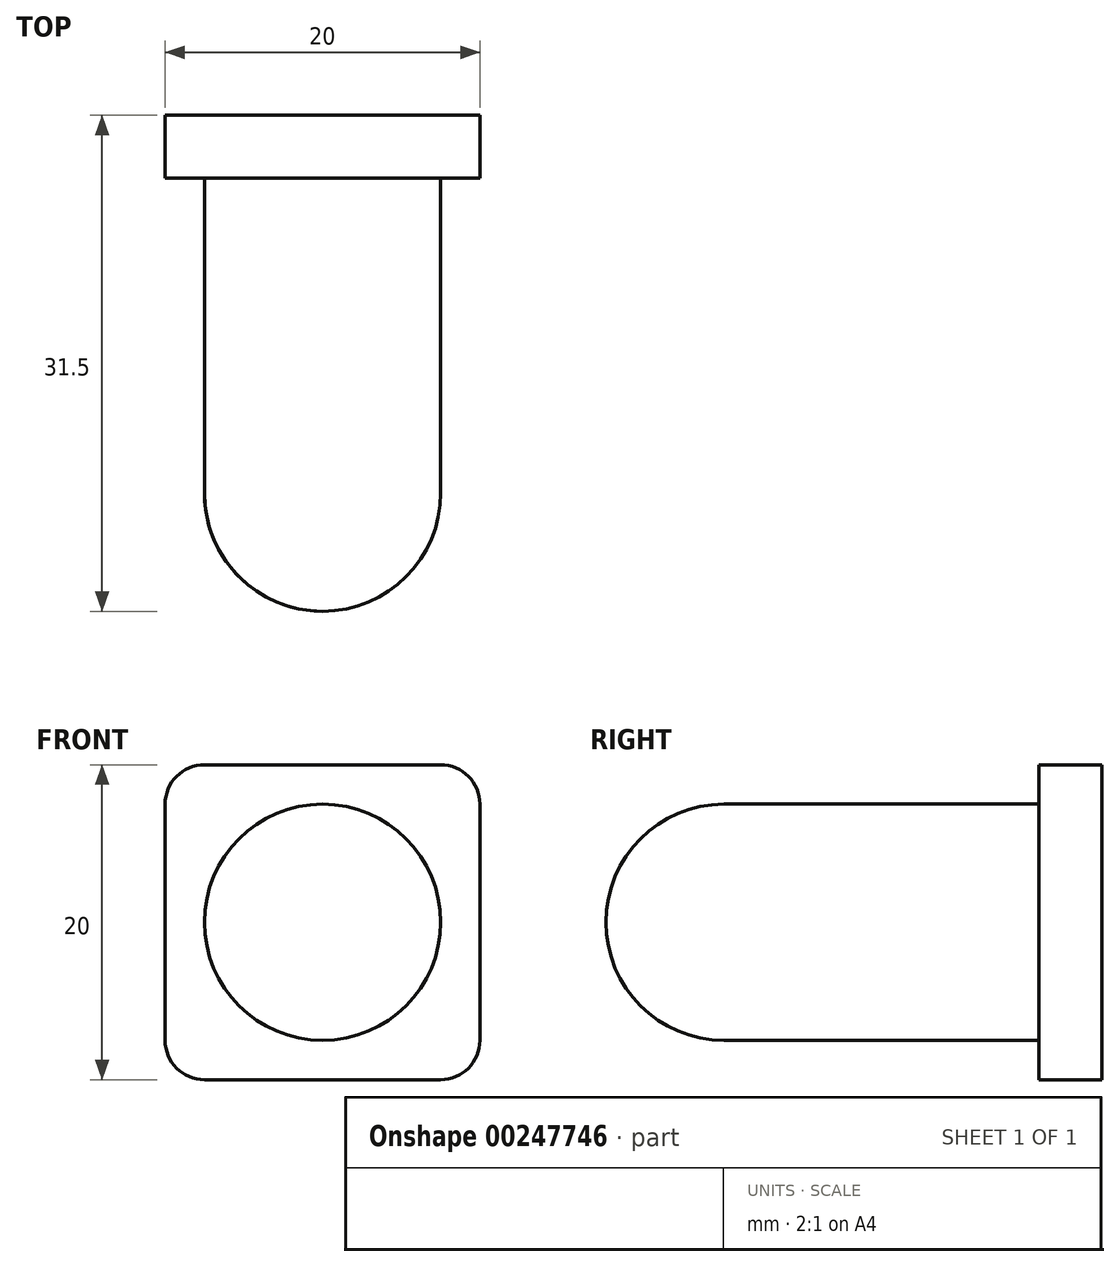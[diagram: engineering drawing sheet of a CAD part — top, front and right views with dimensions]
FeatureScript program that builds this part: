
annotation { "Feature Type Name" : "Feature", "Feature Type Description" : "" }
export const myFeature = defineFeature(function(context is Context, id is Id, definition is map)
    precondition{}
    {
        {
            var Q0;
            Q0=qCreatedBy(makeId("Top.planeOp"),FACE);
            var sketch = newSketch(context, id + "F0", { "sketchPlane" : qUnion([Q0])});
            skCircle(sketch, "E0", {"center": v(0, 0) * mm, "radius": 7.5 * mm});
            skLineSegment(sketch, "E1", {"start": v(-7.5, 0) * mm, "end": v(7.5, 0) * mm});
            skLineSegment(sketch, "E2", {"start": v(0, 0) * mm, "end": v(0, -7.5) * mm});
            skSolve(sketch);
        }
        {
            var Q0;
            {var subQ3=sQuery(id+"F0.wireOp",EDGE,"E2");Q0=makeQuery(id+"F0.imprint","IMPRINT",FACE,{"disambiguationData":[TD([[makeQuery(id+"F0.imprint","IMPRINT",EDGE,{"derivedFrom":subQ3}),1.0]])]});}
            var Q1;
            Q1=sQuery(id+"F0.wireOp",EDGE,"E2");
            revolve(context, id + "F1", {"entities" : qUnion([Q0]), "axis" : qUnion([Q1]), "revolveType" : RevolveType.FULL});
        }
        {
            var Q0;
            Q0=makeQuery(id+"F1.opRevolve","SWEPT_FACE",FACE,{"disambiguationData":[OSD([sQuery(id+"F0.wireOp",EDGE,"E1")])]});
            var sketch = newSketch(context, id + "F2", { "sketchPlane" : qUnion([Q0])});
            skCircle(sketch, "E3", {"center": v(0, 0) * mm, "radius": 7.5 * mm});
            skSolve(sketch);
        }
        {
            var Q0;
            Q0 = qSketchRegion(id + "F2", true);
            extrude(context, id + "F3", {"entities" : qUnion([Q0]), "operationType" : NewBodyOperationType.ADD, "depth" : 20 * mm});
        }
        {
            var Q0;
            Q0=makeQuery(id+"F3.opExtrude","CAP_FACE",FACE,{"disambiguationData":[OSD([sQuery(id+"F2.wireOp",EDGE,"E3")])],"isStart":false});
            var sketch = newSketch(context, id + "F4", { "sketchPlane" : qUnion([Q0])});
            skLineSegment(sketch, "E4.bottom", {"start": v(-10, -10) * mm, "end": v(10, -10) * mm});
            skLineSegment(sketch, "E4.top", {"start": v(-10, 10) * mm, "end": v(10, 10) * mm});
            skLineSegment(sketch, "E4.left", {"start": v(-10, -10) * mm, "end": v(-10, 10) * mm});
            skLineSegment(sketch, "E4.right", {"start": v(10, -10) * mm, "end": v(10, 10) * mm});
            skPoint(sketch, "E4.middle", {"position": v(0, 0) * mm});
            skSolve(sketch);
        }
        {
            var Q0;
            Q0 = qSketchRegion(id + "F4", true);
            extrude(context, id + "F5", {"entities" : qUnion([Q0]), "operationType" : NewBodyOperationType.ADD, "depth" : 4 * mm});
        }
        {
            var Q0;
            Q0=makeQuery(id+"F5.opExtrude","SWEPT_EDGE",EDGE,{"disambiguationData":[OSD([sQuery(id+"F4.wireOp",EDGE,"E4.top"),sQuery(id+"F4.wireOp",EDGE,"E4.right")])]});
            var Q1;
            Q1=makeQuery(id+"F5.opExtrude","SWEPT_EDGE",EDGE,{"disambiguationData":[OSD([sQuery(id+"F4.wireOp",EDGE,"E4.bottom"),sQuery(id+"F4.wireOp",EDGE,"E4.right")])]});
            var Q2;
            Q2=makeQuery(id+"F5.opExtrude","SWEPT_EDGE",EDGE,{"disambiguationData":[OSD([sQuery(id+"F4.wireOp",EDGE,"E4.bottom"),sQuery(id+"F4.wireOp",EDGE,"E4.left")])]});
            var Q3;
            Q3=makeQuery(id+"F5.opExtrude","SWEPT_EDGE",EDGE,{"disambiguationData":[OSD([sQuery(id+"F4.wireOp",EDGE,"E4.top"),sQuery(id+"F4.wireOp",EDGE,"E4.left")])]});
            fillet(context, id + "F6", {"entities" : qUnion([Q0, Q1, Q2, Q3]), "radius" : 2.5 * mm, "tangentPropagation" : true, "allowEdgeOverflow" : false});
        }
    });
